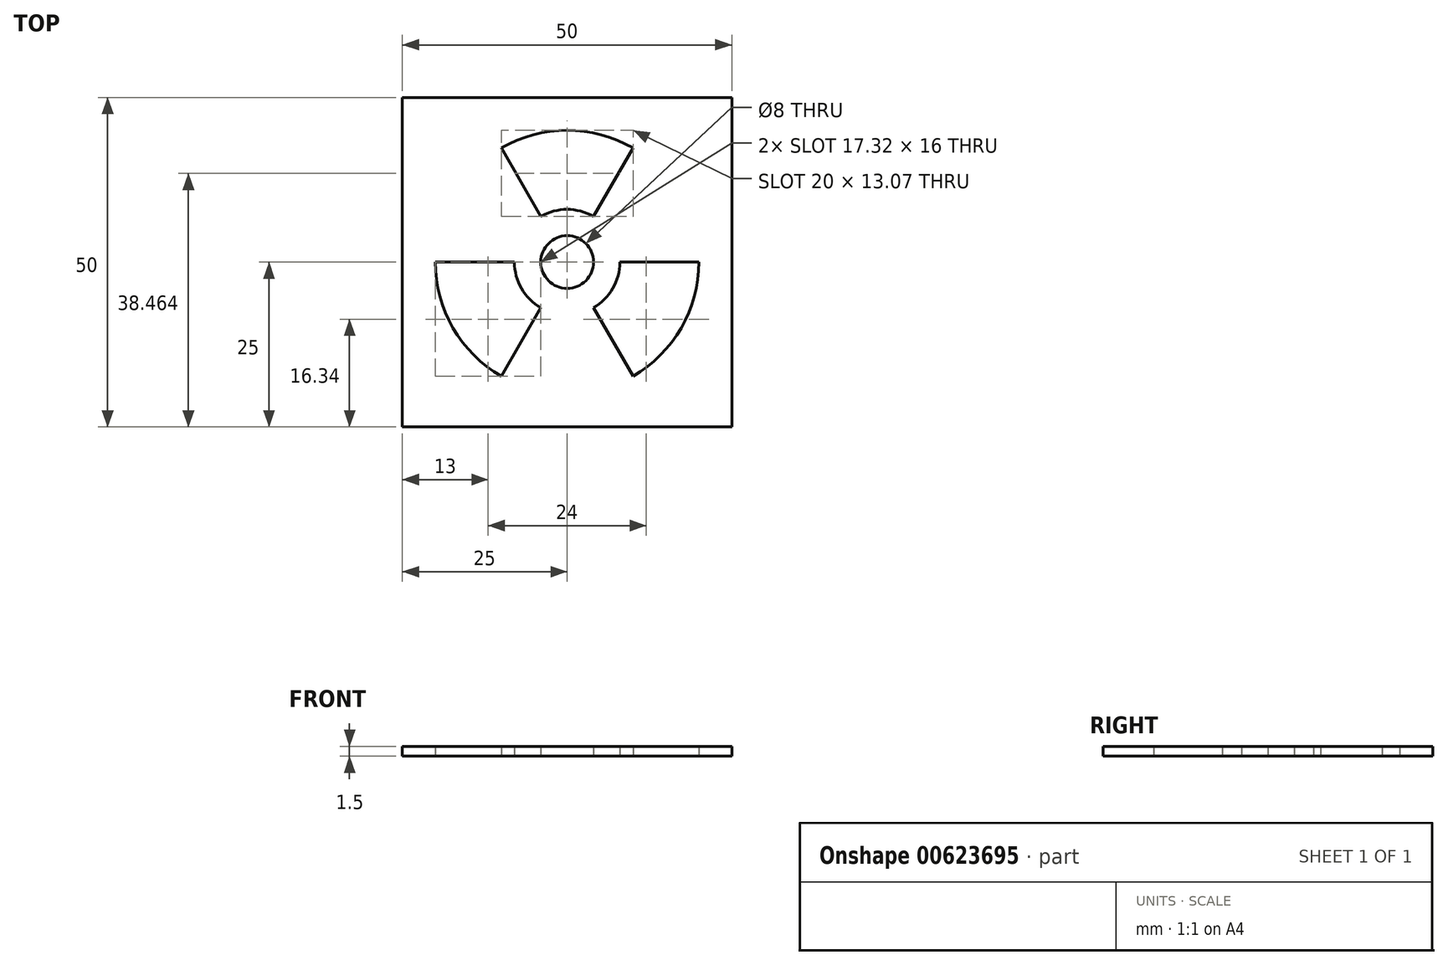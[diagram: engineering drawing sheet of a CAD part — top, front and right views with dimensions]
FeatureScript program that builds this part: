
annotation { "Feature Type Name" : "Feature", "Feature Type Description" : "" }
export const myFeature = defineFeature(function(context is Context, id is Id, definition is map)
    precondition{}
    {
        {
            var Q0;
            Q0=qCreatedBy(makeId("Top.planeOp"),FACE);
            var sketch = newSketch(context, id + "F0", { "sketchPlane" : qUnion([Q0])});
            skLineSegment(sketch, "E0.bottom", {"start": v(-25, 25) * mm, "end": v(25, 25) * mm});
            skLineSegment(sketch, "E0.top", {"start": v(-25, -25) * mm, "end": v(25, -25) * mm});
            skLineSegment(sketch, "E0.left", {"start": v(-25, 25) * mm, "end": v(-25, -25) * mm});
            skLineSegment(sketch, "E0.right", {"start": v(25, 25) * mm, "end": v(25, -25) * mm});
            skLineSegment(sketch, "E1", {"start": v(25, 25) * mm, "end": v(-25, -25) * mm, "construction": true});
            skLineSegment(sketch, "E2", {"start": v(-25, 25) * mm, "end": v(25, -25) * mm, "construction": true});
            skCircle(sketch, "E3", {"center": v(0, 0) * mm, "radius": 4 * mm});
            skLineSegment(sketch, "E4", {"start": v(0, 0) * mm, "end": v(10, 17.32) * mm, "construction": true});
            skLineSegment(sketch, "E5", {"start": v(0, 0) * mm, "end": v(-10, 17.32) * mm, "construction": true});
            skArc(sketch, "E6", {"start": v(10, 17.32) * mm, "mid": v(0, 20) * mm, "end": v(-10, 17.32) * mm});
            skArc(sketch, "E7", {"start": v(4, 6.93) * mm, "mid": v(0, 8) * mm, "end": v(-4, 6.93) * mm});
            skLineSegment(sketch, "E8", {"start": v(-10, 17.32) * mm, "end": v(-4, 6.93) * mm});
            skLineSegment(sketch, "E9", {"start": v(10, 17.32) * mm, "end": v(4, 6.93) * mm});
            skArc(sketch, "E10.1.0", {"start": v(-20, 0) * mm, "mid": v(-17.32, -10) * mm, "end": v(-10, -17.32) * mm});
            skArc(sketch, "E10.1.1", {"start": v(-8, 0) * mm, "mid": v(-6.93, -4) * mm, "end": v(-4, -6.93) * mm});
            skLineSegment(sketch, "E10.1.2", {"start": v(-10, -17.32) * mm, "end": v(-4, -6.93) * mm});
            skLineSegment(sketch, "E10.1.3", {"start": v(-20, 0) * mm, "end": v(-8, 0) * mm});
            skArc(sketch, "E10.2.0", {"start": v(10, -17.32) * mm, "mid": v(17.32, -10) * mm, "end": v(20, 0) * mm});
            skArc(sketch, "E10.2.1", {"start": v(4, -6.93) * mm, "mid": v(6.93, -4) * mm, "end": v(8, 0) * mm});
            skLineSegment(sketch, "E10.2.2", {"start": v(20, 0) * mm, "end": v(8, 0) * mm});
            skLineSegment(sketch, "E10.2.3", {"start": v(10, -17.32) * mm, "end": v(4, -6.93) * mm});
            skSolve(sketch);
        }
        {
            var Q0;
            Q0=makeQuery(id+"F0.imprint","IMPRINT",FACE,{"disambiguationData":[TD([[makeQuery(id+"F0.imprint","IMPRINT",EDGE,{"derivedFrom":sQuery(id+"F0.wireOp",EDGE,"E0.bottom")}),-1.0]])]});
            extrude(context, id + "F1", {"entities" : qUnion([Q0]), "depth" : 1.5 * mm, "offsetDistance" : 25 * mm});
        }
    });
